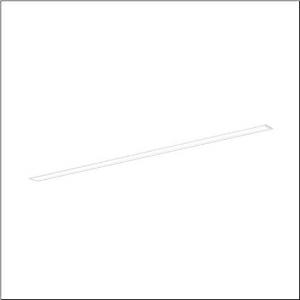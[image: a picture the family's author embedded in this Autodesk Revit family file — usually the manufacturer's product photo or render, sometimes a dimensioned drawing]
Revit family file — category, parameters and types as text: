
# Revit family: silica_r__21_51mx13db45wb_7b80
name_source: partatom
category: Lighting Fixtures
units: mm (PartAtom-declared; Revit-internal decimal feet)

## family parameters
Cut with Voids When Loaded = No
Host = Face
Light Source = No
Part Type = Normal
Room Calculation Point = No
Round Connector Dimension = Use Diameter
Shared = No

## types (1)
- --- (1 x LED, 4100 lm, 28.1 W, 4000K)
    Apparent Load = 28 VA
    CIE Flux Codes = 78 96 99 100 100
    Color Rendering = 80
    Color Temperature = 4000K
    Default Elevation = 1800 mm
    Description = Silica® 21, office luminaire, primary optical cover: prismatic diffuser, of PMMA, CAT 2 (L<= 3000cd/m²), light emission: direct distribution, primary light characteristic: symmetric, installation type: recessed, LED, rated luminous flux: 4.100lm, luminous efficacy: 146lm/W, light colour: 840, colour temperature: 4000K, control gear: DALI 2, with terminal, 3+2-pole, max. 2.5mm², mains connection: 220..240V, AC, 50/60Hz, rated input power: 28.1W, luminaire housing, of aluminium, traffic white (RAL 9016), length: 1.528mm, width: 79mm, height: 53mm, protection rating (complete): IP20, insulation class (complete): insulation class I (protective earthing), certification: CE, ENEC, VDE, permissible operating ambient temperature: 0..+35°C, standard: EN 50419, packaging unit: 1 piece
    Height = 0 mm  [stored 0 ft]
    Lamp = 1 x LED
    Lamp Light Flux = 4100 lm
    Lamp Power = 28.1 W
    Lamp count = 1
    Length = 1527 mm
    Luminous efficacy = 146 lm/W
    Manufacturer = Siteco
    ModVariant = No
    Model = 51MX13DB45WB
    Mounting Place = Ceiling
    Mounting Type = Recessed
    Number of Poles = 1
    OnlyDefault = Yes
    Power Factor = 1
    Product Name = Silica® 21
    Product group = office luminaire | ceiling recessed
    ProductGroupID = 401
    Protection Class = Protection class I
    Protection Degree = IP 20
    RLX_Detail_Level = 1
    RLX_Emergency_Light_Flux = 0 lm
    RLX_Emergency_Type = 0
    RLX_Emergency_Type_DB = No
    RlxData = <blob elided: 14341 chars, md5=18f35e0a>
    Socket = socket
    Standby Power = 0 W
    System Light Flux = 4100 lm
    System Power = 28 W
    Type Comments = factory setting: luminous flux: 100 % | dim-lin: 254 | 323 mA
    Type Image = l_1251692.jpg
    URL = http://relux.com
    VarID = @adj_119086
    Voltage = 0 V
    Weight = 0.00 kg
    Width = 79 mm

note: [stored X ft] marks values corroborated as IEEE doubles in the binary element streams (Revit-internal decimal feet)

## geometry (parser evidence)
native form markers: Sweep x12
no freeform markers — native parametric forms only
